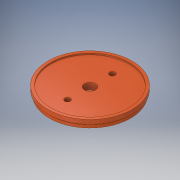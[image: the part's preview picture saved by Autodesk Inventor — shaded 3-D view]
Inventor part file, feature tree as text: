
AUTODESK INVENTOR PART (.ipt)
format: ipt  version: 2017 SP1 (Build 210196100, 196)  size: 148,992 bytes
history: native  units: in
note: dims shown in document units (in); Inventor stores cm internally (conversion verified against a paired STEP export)
features: extrude x5, sketch x5
ambient origin geometry x8: Origin, YZ Plane, XZ Plane, XY Plane, X Axis, Y Axis, Z Axis, Center Point
bodies: Solid1 (feature_tree)
feature tree (10):
  extrude  "Extrusion1"  Depth=0.25in TaperAngle=0.0deg
  extrude  "Extrusion2"  Depth=0.125in TaperAngle=0.0deg
  extrude  "Extrusion3"  Depth=0.25in TaperAngle=0.0deg
  extrude  "Extrusion9"  Depth=7.5in
  extrude  "Extrusion10"  Depth=0.5in
  sketch  "Sketch1"  dims[d0=7.25in d1=0.25in d2=0.0in]
  sketch  "Sketch2"  dims[d3=7.0in d4=0.125in d5=0.0in]
  sketch  "Sketch3"  dims[d6=7.5in d7=0.25in d8=0.0in]
  sketch  "Sketch8"  dims[d33=7.0in d34=7.5in]
  sketch  "Sketch9"  dims[d35=0.125in d36=0.0in d37=0.5in d38=2.0in d39=2.0in d40=1.0in d41=0.125in d42=0.0in]
